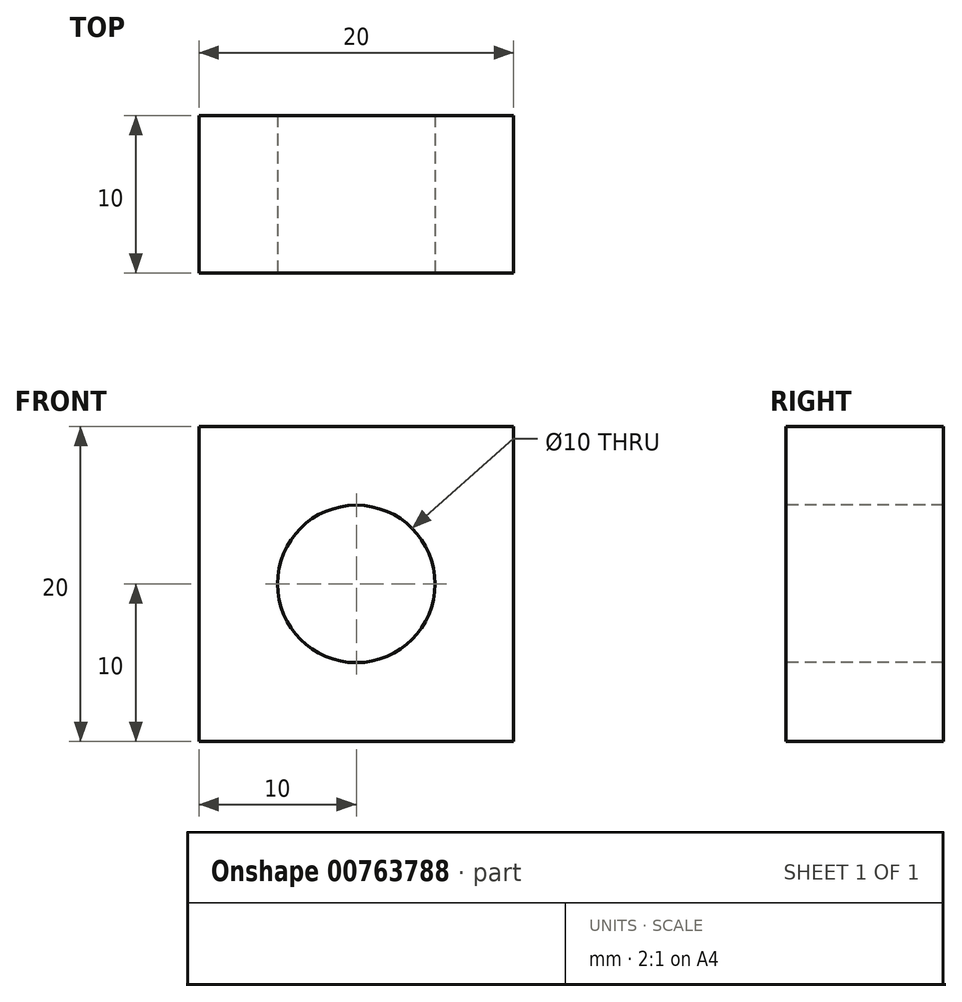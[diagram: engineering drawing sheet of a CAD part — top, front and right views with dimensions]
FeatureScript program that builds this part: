
annotation { "Feature Type Name" : "Feature", "Feature Type Description" : "" }
export const myFeature = defineFeature(function(context is Context, id is Id, definition is map)
    precondition{}
    {
        {
            var Q0;
            Q0=qCreatedBy(makeId("Front.planeOp"),FACE);
            var sketch = newSketch(context, id + "F0", { "sketchPlane" : qUnion([Q0])});
            skLineSegment(sketch, "E0.bottom", {"start": v(10, -10) * mm, "end": v(-10, -10) * mm});
            skLineSegment(sketch, "E0.top", {"start": v(10, 10) * mm, "end": v(-10, 10) * mm});
            skLineSegment(sketch, "E0.left", {"start": v(10, -10) * mm, "end": v(10, 10) * mm});
            skLineSegment(sketch, "E0.right", {"start": v(-10, -10) * mm, "end": v(-10, 10) * mm});
            skPoint(sketch, "E0.middle", {"position": v(0, 0) * mm});
            skSolve(sketch);
        }
        {
            var Q0;
            Q0=makeQuery(id+"F0.imprint","IMPRINT",FACE,{"disambiguationData":[TD([[makeQuery(id+"F0.imprint","IMPRINT",EDGE,{"derivedFrom":sQuery(id+"F0.wireOp",EDGE,"E0.bottom")}),-1.0]])]});
            extrude(context, id + "F1", {"entities" : qUnion([Q0]), "depth" : 10 * mm, "offsetDistance" : 25 * mm});
        }
        {
            var Q0;
            Q0=makeQuery(id+"F1.opExtrude","CAP_FACE",FACE,{"disambiguationData":[OSD([sQuery(id+"F0.wireOp",EDGE,"E0.bottom"),sQuery(id+"F0.wireOp",EDGE,"E0.top"),sQuery(id+"F0.wireOp",EDGE,"E0.left"),sQuery(id+"F0.wireOp",EDGE,"E0.right")])],"isStart":false});
            var sketch = newSketch(context, id + "F2", { "sketchPlane" : qUnion([Q0])});
            skCircle(sketch, "E1", {"center": v(0, 0) * mm, "radius": 5 * mm});
            skSolve(sketch);
        }
        {
            var Q0;
            Q0 = qSketchRegion(id + "F2", true);
            extrude(context, id + "F3", {"entities" : qUnion([Q0]), "operationType" : NewBodyOperationType.REMOVE, "endBound" : BoundingType.THROUGH_ALL, "oppositeDirection" : true, "depth" : 25 * mm, "offsetDistance" : 25 * mm});
        }
    });
